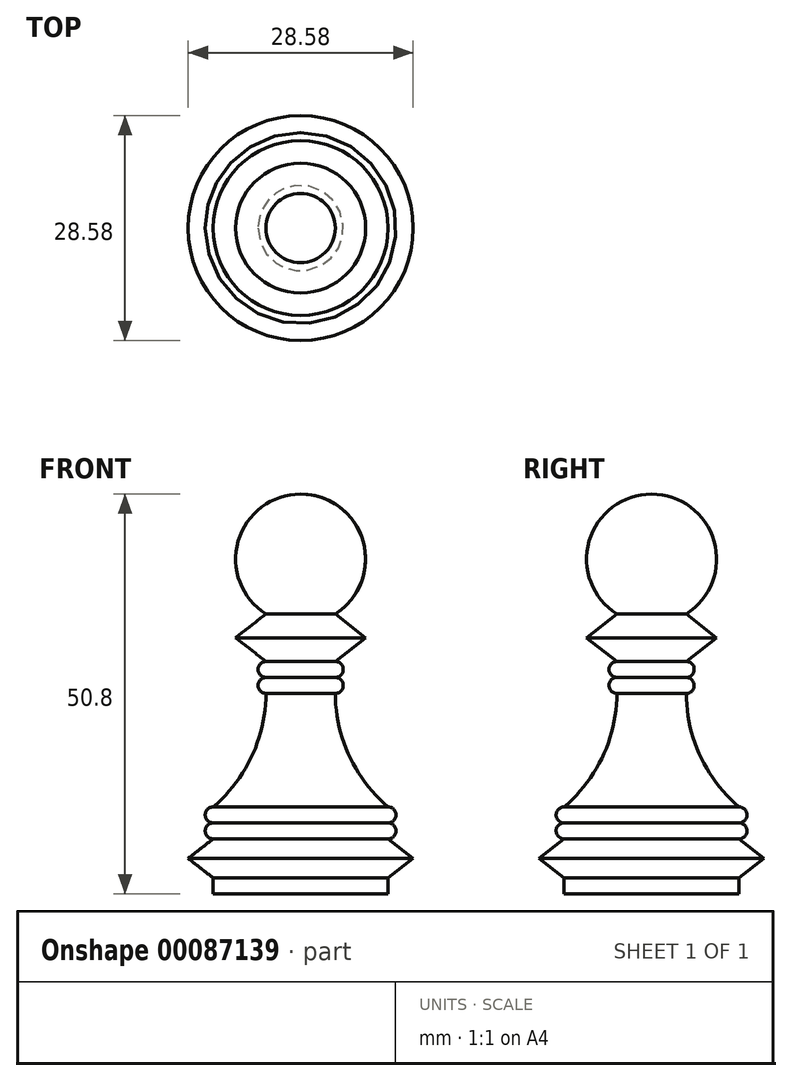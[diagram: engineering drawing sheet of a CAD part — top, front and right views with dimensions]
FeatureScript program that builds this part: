
annotation { "Feature Type Name" : "Feature", "Feature Type Description" : "" }
export const myFeature = defineFeature(function(context is Context, id is Id, definition is map)
    precondition{}
    {
        {
            var Q0;
            Q0=qCreatedBy(makeId("Front.planeOp"),FACE);
            var sketch = newSketch(context, id + "F0", { "sketchPlane" : qUnion([Q0])});
            skLineSegment(sketch, "E0", {"start": v(0, 0) * mm, "end": v(11.11, 0) * mm});
            skLineSegment(sketch, "E1", {"start": v(11.11, 0) * mm, "end": v(11.11, 2.03) * mm});
            skLineSegment(sketch, "E2", {"start": v(11.11, 2.03) * mm, "end": v(14.29, 4.51) * mm});
            skLineSegment(sketch, "E3", {"start": v(14.29, 4.51) * mm, "end": v(11.11, 7) * mm});
            skLineSegment(sketch, "E4", {"start": v(0, 0) * mm, "end": v(0, 50.8) * mm});
            skArc(sketch, "E5", {"start": v(0, 50.8) * mm, "mid": v(7.93, 44.83) * mm, "end": v(4.4, 35.56) * mm});
            skLineSegment(sketch, "E6", {"start": v(4.4, 35.56) * mm, "end": v(8.26, 32.55) * mm});
            skLineSegment(sketch, "E7", {"start": v(8.26, 32.55) * mm, "end": v(4.4, 29.54) * mm});
            skArc(sketch, "E8", {"start": v(4.4, 27.5) * mm, "mid": v(5.42, 28.52) * mm, "end": v(4.4, 29.54) * mm});
            skArc(sketch, "E9", {"start": v(4.4, 25.47) * mm, "mid": v(5.42, 26.49) * mm, "end": v(4.4, 27.5) * mm});
            skArc(sketch, "E10", {"start": v(11.11, 7) * mm, "mid": v(12.13, 8) * mm, "end": v(11.11, 9.03) * mm});
            skArc(sketch, "E11", {"start": v(11.11, 9.03) * mm, "mid": v(12.13, 10.04) * mm, "end": v(11.11, 11.06) * mm});
            skArc(sketch, "E12", {"start": v(4.4, 25.47) * mm, "mid": v(6.18, 17.53) * mm, "end": v(11.11, 11.06) * mm});
            skLineSegment(sketch, "E13", {"start": v(11.11, 7) * mm, "end": v(5.55, 7) * mm, "construction": true});
            skLineSegment(sketch, "E14", {"start": v(11.11, 9.03) * mm, "end": v(6.48, 9.03) * mm, "construction": true});
            skLineSegment(sketch, "E15", {"start": v(4.4, 29.54) * mm, "end": v(2.07, 29.54) * mm, "construction": true});
            skLineSegment(sketch, "E16", {"start": v(4.4, 27.5) * mm, "end": v(2.15, 27.5) * mm, "construction": true});
            skSolve(sketch);
        }
        {
            var Q0;
            Q0 = qSketchRegion(id + "F0", true);
            var Q1;
            Q1=sQuery(id+"F0.wireOp",EDGE,"E4");
            revolve(context, id + "F1", {"entities" : qUnion([Q0]), "axis" : qUnion([Q1]), "revolveType" : RevolveType.FULL});
        }
    });
